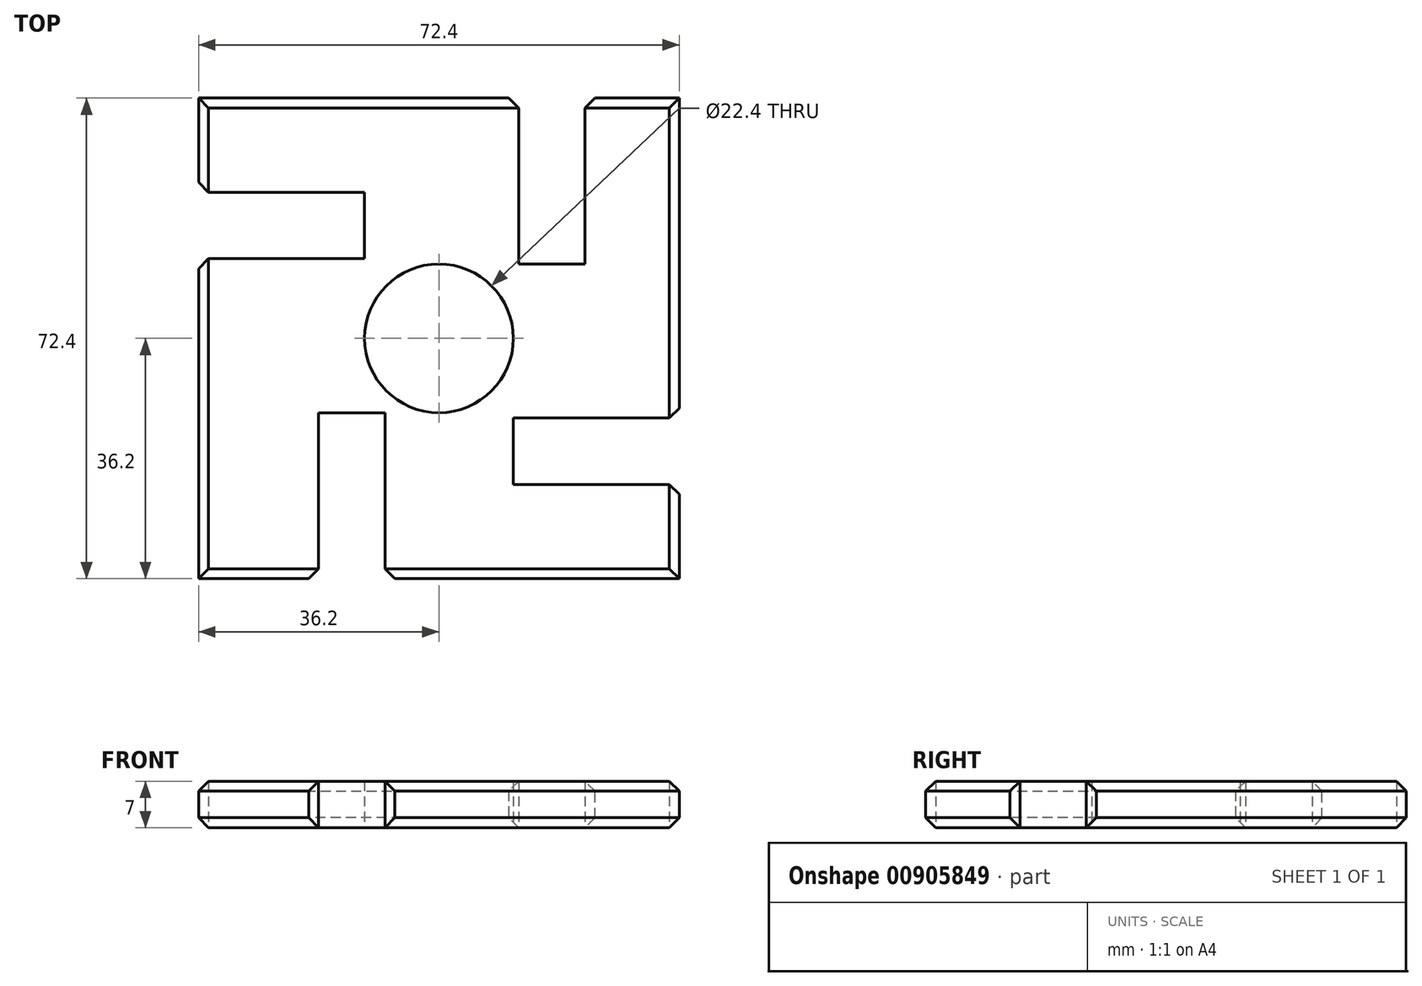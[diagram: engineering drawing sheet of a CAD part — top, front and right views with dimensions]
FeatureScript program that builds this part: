
annotation { "Feature Type Name" : "Feature", "Feature Type Description" : "" }
export const myFeature = defineFeature(function(context is Context, id is Id, definition is map)
    precondition{}
    {
        {
            var Q0;
            Q0=qCreatedBy(makeId("Top.planeOp"),FACE);
            var sketch = newSketch(context, id + "F0", { "sketchPlane" : qUnion([Q0])});
            skCircle(sketch, "E0", {"center": v(0, 0) * mm, "radius": 11.2 * mm});
            skLineSegment(sketch, "E1", {"start": v(-36.2, 0) * mm, "end": v(-36.2, 12) * mm});
            skLineSegment(sketch, "E2", {"start": v(0, 36.2) * mm, "end": v(-36.2, 36.2) * mm});
            skLineSegment(sketch, "E3", {"start": v(-36.2, 0) * mm, "end": v(-36.2, -36.2) * mm});
            skLineSegment(sketch, "E4", {"start": v(0, -36.2) * mm, "end": v(-8.13, -36.2) * mm});
            skLineSegment(sketch, "E5", {"start": v(0, -36.2) * mm, "end": v(36.2, -36.2) * mm});
            skLineSegment(sketch, "E6", {"start": v(36.2, 0) * mm, "end": v(36.2, -12) * mm});
            skLineSegment(sketch, "E7", {"start": v(0, 36.2) * mm, "end": v(12, 36.2) * mm});
            skLineSegment(sketch, "E8", {"start": v(36.2, 36.2) * mm, "end": v(36.2, 0) * mm});
            skLineSegment(sketch, "E9", {"start": v(12, 36.2) * mm, "end": v(12, 11.2) * mm});
            skLineSegment(sketch, "E10", {"start": v(12, 11.2) * mm, "end": v(22, 11.2) * mm});
            skLineSegment(sketch, "E11", {"start": v(22, 11.2) * mm, "end": v(22, 36.2) * mm});
            skLineSegment(sketch, "E12.trimOffspring", {"start": v(22, 36.2) * mm, "end": v(36.2, 36.2) * mm});
            skLineSegment(sketch, "E13", {"start": v(-36.2, 12) * mm, "end": v(-11.2, 12) * mm});
            skLineSegment(sketch, "E14", {"start": v(-11.2, 12) * mm, "end": v(-11.2, 22) * mm});
            skLineSegment(sketch, "E15", {"start": v(-11.2, 22) * mm, "end": v(-36.2, 22) * mm});
            skLineSegment(sketch, "E16.trimOffspring", {"start": v(-36.2, 22) * mm, "end": v(-36.2, 36.2) * mm});
            skLineSegment(sketch, "E17", {"start": v(-8.13, -36.2) * mm, "end": v(-8.13, -11.2) * mm});
            skLineSegment(sketch, "E18", {"start": v(-8.13, -11.2) * mm, "end": v(-18.13, -11.2) * mm});
            skLineSegment(sketch, "E19", {"start": v(-18.13, -11.2) * mm, "end": v(-18.13, -36.2) * mm});
            skLineSegment(sketch, "E20.trimOffspring", {"start": v(-18.13, -36.2) * mm, "end": v(-36.2, -36.2) * mm});
            skLineSegment(sketch, "E21", {"start": v(36.2, -12) * mm, "end": v(11.2, -12) * mm});
            skLineSegment(sketch, "E22", {"start": v(11.2, -12) * mm, "end": v(11.2, -22) * mm});
            skLineSegment(sketch, "E23", {"start": v(11.2, -22) * mm, "end": v(36.2, -22) * mm});
            skLineSegment(sketch, "E24.trimOffspring", {"start": v(36.2, -22) * mm, "end": v(36.2, -36.2) * mm});
            skPoint(sketch, "E25.start.orphan", {"position": v(11.2, 0) * mm});
            skPoint(sketch, "E26.start.orphan", {"position": v(0, -11.2) * mm});
            skPoint(sketch, "E27.start.orphan", {"position": v(-11.2, 0) * mm});
            skPoint(sketch, "E28.start.orphan", {"position": v(0, 11.2) * mm});
            skSolve(sketch);
        }
        {
            var Q0;
            Q0=makeQuery(id+"F0.imprint","IMPRINT",FACE,{"disambiguationData":[TD([[makeQuery(id+"F0.imprint","IMPRINT",EDGE,{"derivedFrom":sQuery(id+"F0.wireOp",EDGE,"E0")}),-1.0]])]});
            extrude(context, id + "F1", {"entities" : qUnion([Q0]), "depth" : 7 * mm, "offsetDistance" : 25 * mm, "symmetric" : true});
        }
        {
            var Q0;
            Q0=makeQuery(id+"F1.opExtrude","CAP_EDGE",EDGE,{"disambiguationData":[OSD([sQuery(id+"F0.wireOp",EDGE,"E4"),sQuery(id+"F0.wireOp",EDGE,"E5")])],"isStart":false});
            var Q1;
            Q1=makeQuery(id+"F1.opExtrude","CAP_EDGE",EDGE,{"disambiguationData":[OSD([sQuery(id+"F0.wireOp",EDGE,"E24.trimOffspring")])],"isStart":false});
            var Q2;
            Q2=makeQuery(id+"F1.opExtrude","CAP_EDGE",EDGE,{"disambiguationData":[OSD([sQuery(id+"F0.wireOp",EDGE,"E6"),sQuery(id+"F0.wireOp",EDGE,"E8")])],"isStart":false});
            var Q3;
            Q3=makeQuery(id+"F1.opExtrude","CAP_EDGE",EDGE,{"disambiguationData":[OSD([sQuery(id+"F0.wireOp",EDGE,"E20.trimOffspring")])],"isStart":false});
            var Q4;
            Q4=makeQuery(id+"F1.opExtrude","CAP_EDGE",EDGE,{"disambiguationData":[OSD([sQuery(id+"F0.wireOp",EDGE,"E1"),sQuery(id+"F0.wireOp",EDGE,"E3")])],"isStart":false});
            var Q5;
            Q5=makeQuery(id+"F1.opExtrude","CAP_EDGE",EDGE,{"disambiguationData":[OSD([sQuery(id+"F0.wireOp",EDGE,"E16.trimOffspring")])],"isStart":false});
            var Q6;
            Q6=makeQuery(id+"F1.opExtrude","CAP_EDGE",EDGE,{"disambiguationData":[OSD([sQuery(id+"F0.wireOp",EDGE,"E2"),sQuery(id+"F0.wireOp",EDGE,"E7")])],"isStart":false});
            var Q7;
            Q7=makeQuery(id+"F1.opExtrude","CAP_EDGE",EDGE,{"disambiguationData":[OSD([sQuery(id+"F0.wireOp",EDGE,"E12.trimOffspring")])],"isStart":false});
            var Q8;
            Q8=makeQuery(id+"F1.opExtrude","CAP_EDGE",EDGE,{"disambiguationData":[OSD([sQuery(id+"F0.wireOp",EDGE,"E24.trimOffspring")])],"isStart":true});
            var Q9;
            Q9=makeQuery(id+"F1.opExtrude","CAP_EDGE",EDGE,{"disambiguationData":[OSD([sQuery(id+"F0.wireOp",EDGE,"E4"),sQuery(id+"F0.wireOp",EDGE,"E5")])],"isStart":true});
            var Q10;
            Q10=makeQuery(id+"F1.opExtrude","CAP_EDGE",EDGE,{"disambiguationData":[OSD([sQuery(id+"F0.wireOp",EDGE,"E6"),sQuery(id+"F0.wireOp",EDGE,"E8")])],"isStart":true});
            var Q11;
            Q11=makeQuery(id+"F1.opExtrude","CAP_EDGE",EDGE,{"disambiguationData":[OSD([sQuery(id+"F0.wireOp",EDGE,"E12.trimOffspring")])],"isStart":true});
            var Q12;
            Q12=makeQuery(id+"F1.opExtrude","CAP_EDGE",EDGE,{"disambiguationData":[OSD([sQuery(id+"F0.wireOp",EDGE,"E2"),sQuery(id+"F0.wireOp",EDGE,"E7")])],"isStart":true});
            var Q13;
            Q13=makeQuery(id+"F1.opExtrude","CAP_EDGE",EDGE,{"disambiguationData":[OSD([sQuery(id+"F0.wireOp",EDGE,"E16.trimOffspring")])],"isStart":true});
            var Q14;
            Q14=makeQuery(id+"F1.opExtrude","CAP_EDGE",EDGE,{"disambiguationData":[OSD([sQuery(id+"F0.wireOp",EDGE,"E1"),sQuery(id+"F0.wireOp",EDGE,"E3")])],"isStart":true});
            var Q15;
            Q15=makeQuery(id+"F1.opExtrude","CAP_EDGE",EDGE,{"disambiguationData":[OSD([sQuery(id+"F0.wireOp",EDGE,"E20.trimOffspring")])],"isStart":true});
            var Q16;
            Q16=makeQuery(id+"F1.opExtrude","SWEPT_EDGE",EDGE,{"disambiguationData":[OSD([sQuery(id+"F0.wireOp",EDGE,"E4"),sQuery(id+"F0.wireOp",EDGE,"E17")])]});
            var Q17;
            Q17=makeQuery(id+"F1.opExtrude","SWEPT_EDGE",EDGE,{"disambiguationData":[OSD([sQuery(id+"F0.wireOp",EDGE,"E19"),sQuery(id+"F0.wireOp",EDGE,"E20.trimOffspring")])]});
            var Q18;
            Q18=makeQuery(id+"F1.opExtrude","SWEPT_EDGE",EDGE,{"disambiguationData":[OSD([sQuery(id+"F0.wireOp",EDGE,"E23"),sQuery(id+"F0.wireOp",EDGE,"E24.trimOffspring")])]});
            var Q19;
            Q19=makeQuery(id+"F1.opExtrude","SWEPT_EDGE",EDGE,{"disambiguationData":[OSD([sQuery(id+"F0.wireOp",EDGE,"E6"),sQuery(id+"F0.wireOp",EDGE,"E21")])]});
            var Q20;
            Q20=makeQuery(id+"F1.opExtrude","SWEPT_EDGE",EDGE,{"disambiguationData":[OSD([sQuery(id+"F0.wireOp",EDGE,"E11"),sQuery(id+"F0.wireOp",EDGE,"E12.trimOffspring")])]});
            var Q21;
            Q21=makeQuery(id+"F1.opExtrude","SWEPT_EDGE",EDGE,{"disambiguationData":[OSD([sQuery(id+"F0.wireOp",EDGE,"E7"),sQuery(id+"F0.wireOp",EDGE,"E9")])]});
            var Q22;
            Q22=makeQuery(id+"F1.opExtrude","SWEPT_EDGE",EDGE,{"disambiguationData":[OSD([sQuery(id+"F0.wireOp",EDGE,"E15"),sQuery(id+"F0.wireOp",EDGE,"E16.trimOffspring")])]});
            var Q23;
            Q23=makeQuery(id+"F1.opExtrude","SWEPT_EDGE",EDGE,{"disambiguationData":[OSD([sQuery(id+"F0.wireOp",EDGE,"E1"),sQuery(id+"F0.wireOp",EDGE,"E13")])]});
            chamfer(context, id + "F2", {"entities" : qUnion([Q0, Q1, Q2, Q3, Q4, Q5, Q6, Q7, Q8, Q9, Q10, Q11, Q12, Q13, Q14, Q15, Q16, Q17, Q18, Q19, Q20, Q21, Q22, Q23]), "width" : 1.5 * mm, "tangentPropagation" : true});
        }
    });
